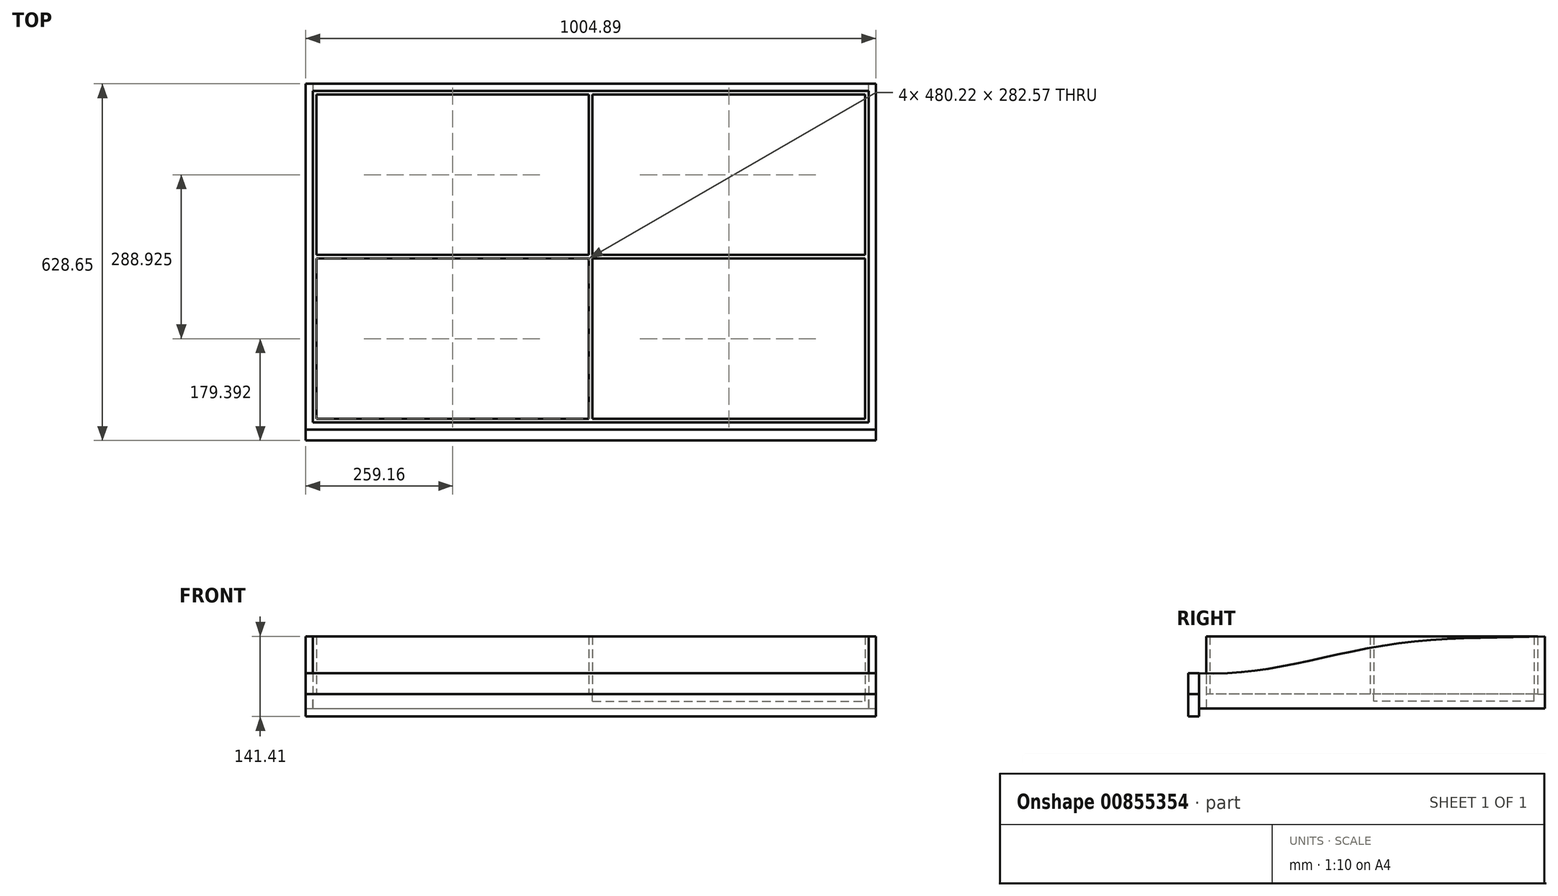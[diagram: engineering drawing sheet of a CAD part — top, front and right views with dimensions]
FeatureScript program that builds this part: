
annotation { "Feature Type Name" : "Feature", "Feature Type Description" : "" }
export const myFeature = defineFeature(function(context is Context, id is Id, definition is map)
    precondition{}
    {
        {
            var Q0;
            Q0=qCreatedBy(makeId("Top.planeOp"),FACE);
            var sketch = newSketch(context, id + "F0", { "sketchPlane" : qUnion([Q0])});
            skLineSegment(sketch, "E0.bottom", {"start": v(-87.02, 553.73) * mm, "end": v(917.87, 553.73) * mm});
            skLineSegment(sketch, "E0.top", {"start": v(-87.02, -55.87) * mm, "end": v(917.87, -55.87) * mm});
            skLineSegment(sketch, "E0.left", {"start": v(-87.02, 553.73) * mm, "end": v(-87.02, -55.87) * mm});
            skLineSegment(sketch, "E0.right", {"start": v(917.87, 553.73) * mm, "end": v(917.87, -55.87) * mm});
            skLineSegment(sketch, "E1.0", {"start": v(-74.32, 541.03) * mm, "end": v(905.17, 541.03) * mm});
            skLineSegment(sketch, "E1.1", {"start": v(-74.32, 541.03) * mm, "end": v(-74.32, -43.17) * mm});
            skLineSegment(sketch, "E1.2", {"start": v(-74.32, -43.17) * mm, "end": v(905.17, -43.17) * mm});
            skLineSegment(sketch, "E1.3", {"start": v(905.17, 541.03) * mm, "end": v(905.17, -43.17) * mm});
            skLineSegment(sketch, "E2.top", {"start": v(-87.02, -74.92) * mm, "end": v(917.87, -74.92) * mm});
            skLineSegment(sketch, "E2.left", {"start": v(-87.02, -55.87) * mm, "end": v(-87.02, -74.92) * mm});
            skLineSegment(sketch, "E2.right", {"start": v(917.87, -55.87) * mm, "end": v(917.87, -74.92) * mm});
            skLineSegment(sketch, "E3.0", {"start": v(-67.97, 534.68) * mm, "end": v(412.25, 534.68) * mm});
            skLineSegment(sketch, "E3.1", {"start": v(-67.97, 534.68) * mm, "end": v(-67.97, 252.1) * mm});
            skLineSegment(sketch, "E3.2", {"start": v(-67.97, -36.82) * mm, "end": v(412.25, -36.82) * mm});
            skLineSegment(sketch, "E3.3", {"start": v(898.82, 534.68) * mm, "end": v(898.82, 252.1) * mm});
            skLineSegment(sketch, "E4", {"start": v(898.82, 245.76) * mm, "end": v(418.6, 245.76) * mm});
            skLineSegment(sketch, "E5.0", {"start": v(898.82, 252.1) * mm, "end": v(418.6, 252.1) * mm});
            skLineSegment(sketch, "E6", {"start": v(412.25, -36.82) * mm, "end": v(412.25, 245.76) * mm});
            skLineSegment(sketch, "E7", {"start": v(412.25, 252.1) * mm, "end": v(412.25, 534.68) * mm});
            skLineSegment(sketch, "E8.0", {"start": v(418.6, 252.1) * mm, "end": v(418.6, 534.68) * mm});
            skLineSegment(sketch, "E9.0", {"start": v(418.6, -36.82) * mm, "end": v(418.6, 245.76) * mm});
            skLineSegment(sketch, "E10.trimOffspring", {"start": v(412.25, 252.1) * mm, "end": v(-67.97, 252.1) * mm});
            skLineSegment(sketch, "E11.trimOffspring", {"start": v(412.25, 245.76) * mm, "end": v(-67.97, 245.76) * mm});
            skLineSegment(sketch, "E12.trimOffspring", {"start": v(418.6, -36.82) * mm, "end": v(898.82, -36.82) * mm});
            skLineSegment(sketch, "E13.trimOffspring", {"start": v(898.82, 245.76) * mm, "end": v(898.82, -36.82) * mm});
            skLineSegment(sketch, "E14.trimOffspring", {"start": v(-67.97, 245.76) * mm, "end": v(-67.97, -36.82) * mm});
            skLineSegment(sketch, "E15.trimOffspring", {"start": v(418.6, 534.68) * mm, "end": v(898.82, 534.68) * mm});
            skLineSegment(sketch, "E16", {"start": v(905.17, 541.03) * mm, "end": v(905.17, 553.73) * mm});
            skLineSegment(sketch, "E17", {"start": v(-74.32, 541.03) * mm, "end": v(-74.32, 553.73) * mm});
            skLineSegment(sketch, "E18", {"start": v(412.25, -36.82) * mm, "end": v(418.6, -36.82) * mm});
            skSolve(sketch);
        }
        {
            var Q0;
            Q0=makeQuery(id+"F0.imprint","IMPRINT",FACE,{"disambiguationData":[TD([[makeQuery(id+"F0.imprint","IMPRINT",EDGE,{"derivedFrom":sQuery(id+"F0.wireOp",EDGE,"E0.bottom")}),-1.0]])]});
            var Q1;
            Q1=makeQuery(id+"F0.imprint","IMPRINT",FACE,{"disambiguationData":[TD([[makeQuery(id+"F0.imprint","IMPRINT",EDGE,{"derivedFrom":sQuery(id+"F0.wireOp",EDGE,"E1.0")}),1.0]])]});
            extrude(context, id + "F1", {"entities" : qUnion([Q0, Q1]), "depth" : 101.6 * mm, "offsetDistance" : 25.4 * mm});
        }
        {
            var Q0;
            Q0=makeQuery(id+"F0.imprint","IMPRINT",FACE,{"disambiguationData":[TD([[makeQuery(id+"F0.imprint","IMPRINT",EDGE,{"derivedFrom":sQuery(id+"F0.wireOp",EDGE,"E0.top")}),1.0]])]});
            extrude(context, id + "F2", {"entities" : qUnion([Q0]), "operationType" : NewBodyOperationType.ADD, "oppositeDirection" : true, "depth" : 25.4 * mm, "offsetDistance" : 25.4 * mm});
        }
        {
            var Q0;
            Q0=makeQuery(id+"F0.imprint","IMPRINT",FACE,{"disambiguationData":[TD([[makeQuery(id+"F0.imprint","IMPRINT",EDGE,{"derivedFrom":sQuery(id+"F0.wireOp",EDGE,"E3.3")}),-1.0]])]});
            var sketch = newSketch(context, id + "F3", { "sketchPlane" : qUnion([Q0])});
            skLineSegment(sketch, "E19.0", {"start": v(-87.02, 553.73) * mm, "end": v(-87.02, -55.87) * mm});
            skLineSegment(sketch, "E20.0", {"start": v(-87.02, -55.87) * mm, "end": v(917.87, -55.87) * mm});
            skLineSegment(sketch, "E21.0", {"start": v(917.87, 553.73) * mm, "end": v(917.87, -55.87) * mm});
            skLineSegment(sketch, "E22.0", {"start": v(-87.02, 553.73) * mm, "end": v(917.87, 553.73) * mm});
            skLineSegment(sketch, "E23.left", {"start": v(-87.02, -55.87) * mm, "end": v(-87.02, 553.73) * mm});
            skLineSegment(sketch, "E23.right", {"start": v(917.87, -55.87) * mm, "end": v(917.87, 553.73) * mm});
            skSolve(sketch);
        }
        {
            var Q0;
            Q0=makeQuery(id+"F3.imprint","IMPRINT",FACE,{"disambiguationData":[TD([[makeQuery(id+"F3.imprint","IMPRINT",EDGE,{"derivedFrom":sQuery(id+"F3.wireOp",EDGE,"E20.0")}),1.0]])]});
            var Q1;
            Q1=makeQuery(id+"F3.imprint","IMPRINT",FACE,{"disambiguationData":[TD([[makeQuery(id+"F3.imprint","IMPRINT",EDGE,{"derivedFrom":makeQuery(id+"F0.imprint","IMPRINT",EDGE,{"derivedFrom":sQuery(id+"F0.wireOp",EDGE,"E3.3")})}),-1.0]])]});
            extrude(context, id + "F4", {"entities" : qUnion([Q0, Q1]), "operationType" : NewBodyOperationType.ADD, "oppositeDirection" : true, "depth" : 12.7 * mm, "offsetDistance" : 25.4 * mm});
        }
        {
            var Q0;
            {var subQ0=sQuery(id+"F0.wireOp",EDGE,"E0.left");Q0=makeQuery(id+"F2.boolean.opBoolean","MERGE",FACE,{"derivedFrom":[makeQuery(id+"F1.opExtrude","SWEPT_FACE",FACE,{"disambiguationData":[OSD([subQ0])]}),makeQuery(id+"F2.opExtrude","SWEPT_FACE",FACE,{"disambiguationData":[OSD([subQ0])]})]});}
            var sketch = newSketch(context, id + "F5", { "sketchPlane" : qUnion([Q0])});
            skFitSpline(sketch, "E24", {"points": [v(-553.73, 101.6) * mm, v(-316.27, 91.73) * mm, v(-113.67, 53.29) * mm, v(55.87, 36.51) * mm], "startDerivative": vector(622.37, -26.3) * mm, "endDerivative": vector(608.29, 23.06) * mm});
            skLineSegment(sketch, "E25", {"start": v(-553.73, 101.6) * mm, "end": v(55.87, 101.6) * mm});
            skLineSegment(sketch, "E26", {"start": v(55.87, 101.6) * mm, "end": v(55.87, 36.51) * mm});
            skSolve(sketch);
        }
        {
            var Q0;
            Q0=makeQuery(id+"F5.imprint","IMPRINT",FACE,{"disambiguationData":[TD([[makeQuery(id+"F5.imprint","IMPRINT",EDGE,{"derivedFrom":sQuery(id+"F5.wireOp",EDGE,"E24")}),1.0]])]});
            extrude(context, id + "F6", {"entities" : qUnion([Q0]), "operationType" : NewBodyOperationType.REMOVE, "endBound" : BoundingType.THROUGH_ALL, "oppositeDirection" : true, "depth" : 25.4 * mm, "offsetDistance" : 25.4 * mm});
        }
        {
            var Q0;
            Q0=makeQuery(id+"F0.imprint","IMPRINT",FACE,{"disambiguationData":[TD([[makeQuery(id+"F0.imprint","IMPRINT",EDGE,{"derivedFrom":sQuery(id+"F0.wireOp",EDGE,"E0.top")}),-1.0]])]});
            extrude(context, id + "F7", {"entities" : qUnion([Q0]), "depth" : 36.5 * mm, "offsetDistance" : 25.4 * mm});
        }
        {
            var Q0;
            Q0=makeQuery(id+"F0.imprint","IMPRINT",FACE,{"disambiguationData":[TD([[makeQuery(id+"F0.imprint","IMPRINT",EDGE,{"derivedFrom":sQuery(id+"F0.wireOp",EDGE,"E0.top")}),-1.0]])]});
            extrude(context, id + "F8", {"entities" : qUnion([Q0]), "oppositeDirection" : true, "depth" : 39.81 * mm, "offsetDistance" : 25.4 * mm});
        }
        {
            var Q0;
            Q0=makeQuery(id+"F0.imprint","IMPRINT",FACE,{"disambiguationData":[TD([[makeQuery(id+"F0.imprint","IMPRINT",EDGE,{"derivedFrom":sQuery(id+"F0.wireOp",EDGE,"E1.0")}),-1.0]])]});
            extrude(context, id + "F9", {"entities" : qUnion([Q0]), "depth" : 101.6 * mm, "offsetDistance" : 25.4 * mm});
        }
    });
